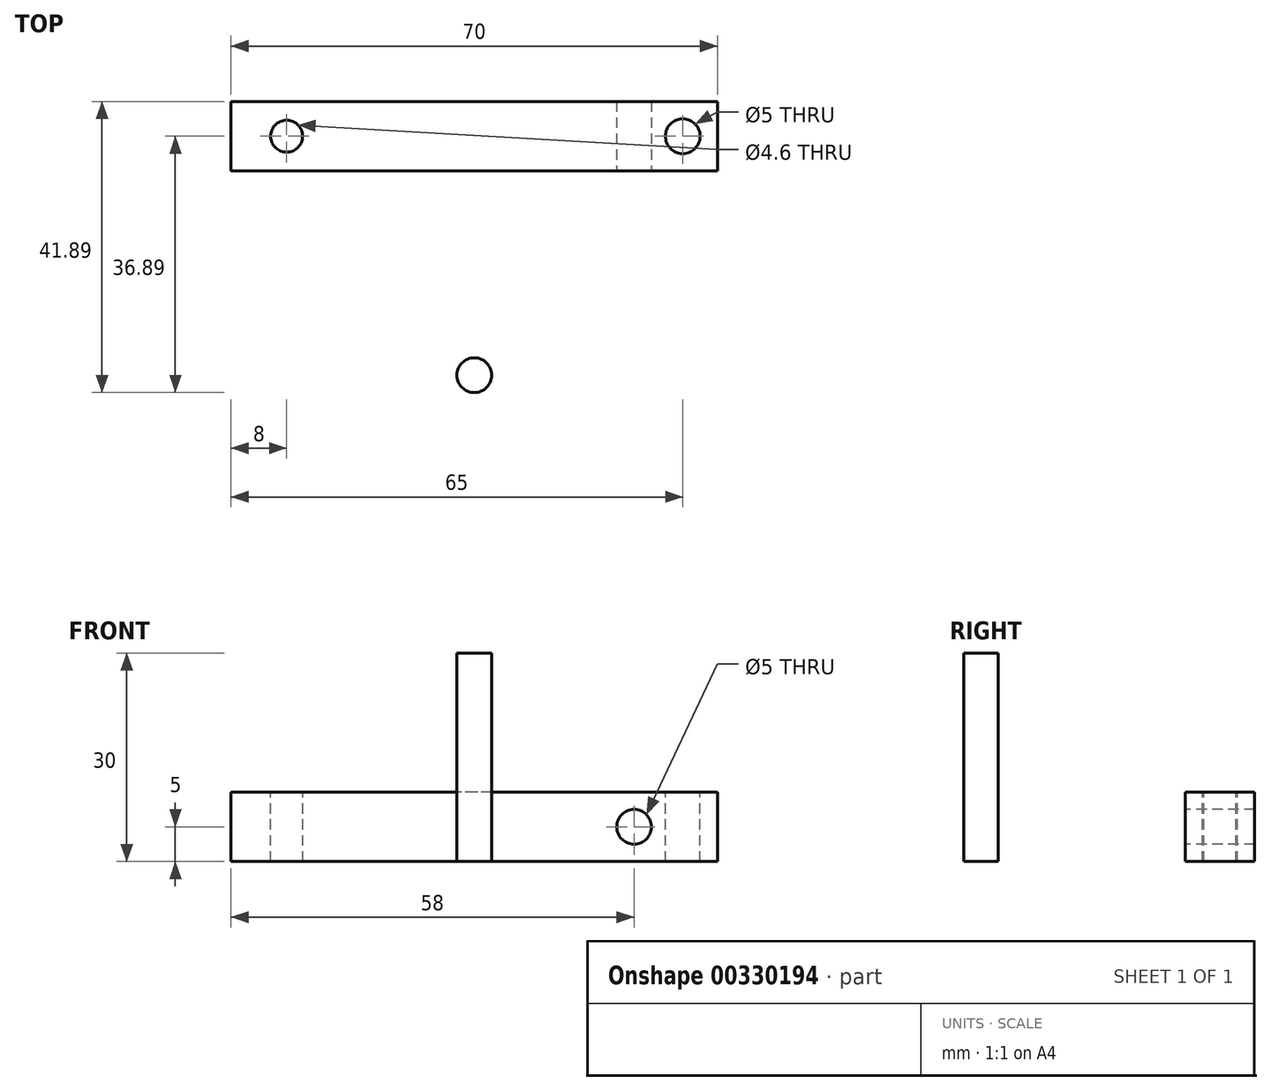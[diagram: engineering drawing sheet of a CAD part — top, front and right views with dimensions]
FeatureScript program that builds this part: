
annotation { "Feature Type Name" : "Feature", "Feature Type Description" : "" }
export const myFeature = defineFeature(function(context is Context, id is Id, definition is map)
    precondition{}
    {
        {
            var Q0;
            Q0=qCreatedBy(makeId("Top.planeOp"),FACE);
            var sketch = newSketch(context, id + "F0", { "sketchPlane" : qUnion([Q0])});
            skLineSegment(sketch, "E0.bottom", {"start": v(35, -5) * mm, "end": v(-35, -5) * mm});
            skLineSegment(sketch, "E0.top", {"start": v(35, 5) * mm, "end": v(-35, 5) * mm});
            skLineSegment(sketch, "E0.left", {"start": v(35, -5) * mm, "end": v(35, 5) * mm});
            skLineSegment(sketch, "E0.right", {"start": v(-35, -5) * mm, "end": v(-35, 5) * mm});
            skPoint(sketch, "E0.middle", {"position": v(0, 0) * mm});
            skSolve(sketch);
        }
        {
            var Q0;
            Q0 = qSketchRegion(id + "F0", true);
            extrude(context, id + "F1", {"entities" : qUnion([Q0]), "depth" : 10 * mm});
        }
        {
            var Q0;
            Q0=makeQuery(id+"F1.opExtrude","SWEPT_FACE",FACE,{"disambiguationData":[OSD([sQuery(id+"F0.wireOp",EDGE,"E0.bottom")])]});
            var sketch = newSketch(context, id + "F2", { "sketchPlane" : qUnion([Q0])});
            skCircle(sketch, "E1", {"center": v(23, 5) * mm, "radius": 2.5 * mm});
            skPoint(sketch, "E1.centerSnap0", {"position": v(35, 5) * mm});
            skSolve(sketch);
        }
        {
            var Q0;
            Q0 = qSketchRegion(id + "F2", true);
            extrude(context, id + "F3", {"entities" : qUnion([Q0]), "operationType" : NewBodyOperationType.REMOVE, "oppositeDirection" : true, "depth" : 25 * mm});
        }
        {
            var Q0;
            Q0=makeQuery(id+"F1.opExtrude","CAP_FACE",FACE,{"disambiguationData":[OSD([sQuery(id+"F0.wireOp",EDGE,"E0.bottom"),sQuery(id+"F0.wireOp",EDGE,"E0.top"),sQuery(id+"F0.wireOp",EDGE,"E0.left"),sQuery(id+"F0.wireOp",EDGE,"E0.right")])],"isStart":false});
            var sketch = newSketch(context, id + "F4", { "sketchPlane" : qUnion([Q0])});
            skPoint(sketch, "E2", {"position": v(-27, 0) * mm});
            skPoint(sketch, "E3", {"position": v(30, 0) * mm});
            skSolve(sketch);
        }
        {
            var Q0;
            Q0=sQuery(id+"F4.wireOp",VERTEX,"E3");
            var Q1;
            Q1=makeQuery(id+"F1.opExtrude","SWEPT_BODY",BODY,{"disambiguationData":[OSD([sQuery(id+"F0.wireOp",EDGE,"E0.bottom"),sQuery(id+"F0.wireOp",EDGE,"E0.top"),sQuery(id+"F0.wireOp",EDGE,"E0.left"),sQuery(id+"F0.wireOp",EDGE,"E0.right")])]});
            hole(context, id + "F5", {"style" : HoleStyle.SIMPLE, "endStyle" : HoleEndStyle.THROUGH, "standardTappedOrClearance" : lookupTablePath({ "standard" : "ISO", "engagement" : "75%", "pitch" : "1 mm", "size" : "M6", "type" : "Tapped" }), "standardBlindInLast" : lookupTablePath({ "standard" : "ISO", "engagement" : "75%", "pitch" : "1 mm", "size" : "M6", "type" : "Tapped" }), "holeDiameter" : 5 * mm, "showTappedDepth" : true, "tappedDepth" : 9 * mm, "tapClearance" : 3, "locations" : qUnion([Q0]), "scope" : qUnion([Q1]), "majorDiameter" : 6 * mm});
        }
        {
            var Q0;
            Q0=sQuery(id+"F4.wireOp",VERTEX,"E2");
            var Q1;
            Q1=makeQuery(id+"F1.opExtrude","SWEPT_BODY",BODY,{"disambiguationData":[OSD([sQuery(id+"F0.wireOp",EDGE,"E0.bottom"),sQuery(id+"F0.wireOp",EDGE,"E0.top"),sQuery(id+"F0.wireOp",EDGE,"E0.left"),sQuery(id+"F0.wireOp",EDGE,"E0.right")])]});
            hole(context, id + "F6", {"style" : HoleStyle.SIMPLE, "endStyle" : HoleEndStyle.THROUGH, "holeDiameter" : 4.6 * mm, "tappedDepth" : 9 * mm, "tapClearance" : 3, "locations" : qUnion([Q0]), "scope" : qUnion([Q1])});
        }
        {
            var Q0;
            Q0=qCreatedBy(makeId("Top.planeOp"),FACE);
            var sketch = newSketch(context, id + "F7", { "sketchPlane" : qUnion([Q0])});
            skCircle(sketch, "E4", {"center": v(0, -34.4) * mm, "radius": 2.5 * mm});
            skSolve(sketch);
        }
        {
            var Q0;
            Q0 = qSketchRegion(id + "F7", true);
            extrude(context, id + "F8", {"entities" : qUnion([Q0]), "depth" : 30 * mm});
        }
    });
